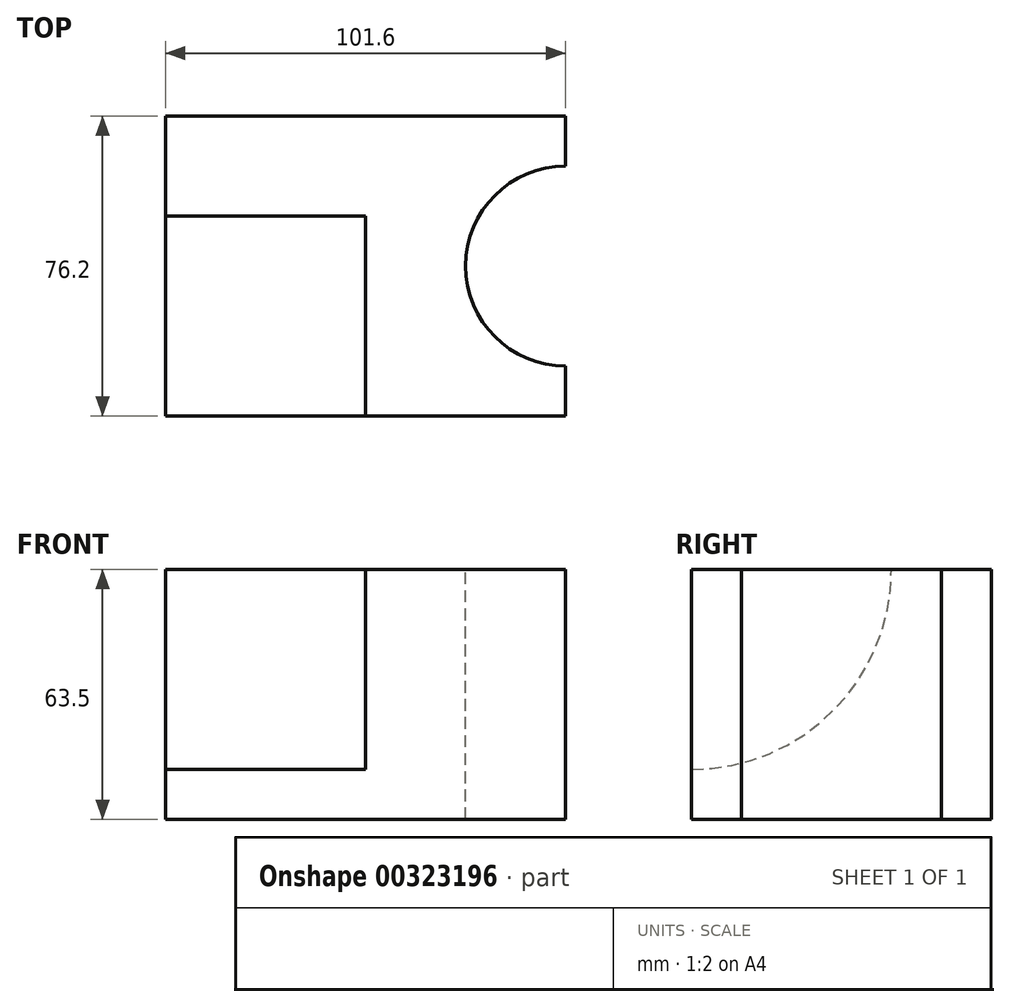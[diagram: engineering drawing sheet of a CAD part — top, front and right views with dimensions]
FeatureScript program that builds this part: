
annotation { "Feature Type Name" : "Feature", "Feature Type Description" : "" }
export const myFeature = defineFeature(function(context is Context, id is Id, definition is map)
    precondition{}
    {
        {
            var Q0;
            Q0=qCreatedBy(makeId("Front.planeOp"),FACE);
            var sketch = newSketch(context, id + "F0", { "sketchPlane" : qUnion([Q0])});
            skLineSegment(sketch, "E0", {"start": v(-51.32, -42.94) * mm, "end": v(50.28, -42.94) * mm});
            skLineSegment(sketch, "E1", {"start": v(50.28, -42.94) * mm, "end": v(50.28, 20.56) * mm});
            skLineSegment(sketch, "E2", {"start": v(50.28, 20.56) * mm, "end": v(-51.32, 20.56) * mm});
            skLineSegment(sketch, "E3", {"start": v(-51.32, 20.56) * mm, "end": v(-51.32, -42.94) * mm});
            skSolve(sketch);
        }
        {
            var Q0;
            Q0 = qSketchRegion(id + "F0", true);
            extrude(context, id + "F1", {"entities" : qUnion([Q0]), "oppositeDirection" : true, "depth" : 76.2 * mm});
        }
        {
            var Q0;
            Q0=makeQuery(id+"F1.opExtrude","SWEPT_FACE",FACE,{"disambiguationData":[OSD([sQuery(id+"F0.wireOp",EDGE,"E2")])]});
            var sketch = newSketch(context, id + "F2", { "sketchPlane" : qUnion([Q0])});
            skCircle(sketch, "E4", {"center": v(50.28, 38.1) * mm, "radius": 25.4 * mm});
            skSolve(sketch);
        }
        {
            var Q0;
            {var subQ0=sQuery(id+"F2.wireOp",EDGE,"E4");var subQ1=makeQuery(id+"F1.opExtrude","SWEPT_EDGE",EDGE,{"disambiguationData":[OSD([sQuery(id+"F0.wireOp",EDGE,"E1"),sQuery(id+"F0.wireOp",EDGE,"E2")])]});var subQ2=makeQuery(id+"F2.imprint","INTERSECT",VERTEX,{"disambiguationData":[OD(0.0)],"derivedFrom":[subQ1,subQ0]});Q0=makeQuery(id+"F2.imprint","IMPRINT",FACE,{"disambiguationData":[TD([[makeQuery(id+"F2.imprint","IMPRINT",EDGE,{"disambiguationData":[TD([[subQ2,-1.0]])],"derivedFrom":subQ0}),1.0]])]});}
            var Q1;
            {var subQ0=sQuery(id+"F2.wireOp",EDGE,"E4");var subQ1=makeQuery(id+"F1.opExtrude","SWEPT_EDGE",EDGE,{"disambiguationData":[OSD([sQuery(id+"F0.wireOp",EDGE,"E1"),sQuery(id+"F0.wireOp",EDGE,"E2")])]});var subQ2=makeQuery(id+"F2.imprint","INTERSECT",VERTEX,{"disambiguationData":[OD(0.0)],"derivedFrom":[subQ1,subQ0]});Q1=makeQuery(id+"F2.imprint","IMPRINT",FACE,{"disambiguationData":[TD([[makeQuery(id+"F2.imprint","IMPRINT",EDGE,{"disambiguationData":[TD([[subQ2,1.0]])],"derivedFrom":subQ0}),1.0]])]});}
            var Q2;
            Q2=sQuery(id+"F2.wireOp",EDGE,"E4");
            extrude(context, id + "F3", {"entities" : qUnion([Q0, Q1]), "operationType" : NewBodyOperationType.REMOVE, "surfaceEntities" : qUnion([Q2]), "oppositeDirection" : true, "depth" : 63.5 * mm});
        }
        {
            var Q0;
            Q0=makeQuery(id+"F1.opExtrude","SWEPT_FACE",FACE,{"disambiguationData":[OSD([sQuery(id+"F0.wireOp",EDGE,"E3")])]});
            var sketch = newSketch(context, id + "F4", { "sketchPlane" : qUnion([Q0])});
            skCircle(sketch, "E5", {"center": v(0, 20.56) * mm, "radius": 50.8 * mm});
            skSolve(sketch);
        }
        {
            var Q0;
            {var subQ0=sQuery(id+"F4.wireOp",EDGE,"E5");var subQ1=sQuery(id+"F0.wireOp",EDGE,"E3");var subQ4=makeQuery(id+"F1.opExtrude","CAP_EDGE",EDGE,{"disambiguationData":[OSD([subQ1])],"isStart":true});var subQ5=makeQuery(id+"F4.imprint","INTERSECT",VERTEX,{"derivedFrom":[subQ4,subQ0]});Q0=makeQuery(id+"F4.imprint","IMPRINT",FACE,{"disambiguationData":[TD([[makeQuery(id+"F4.imprint","IMPRINT",EDGE,{"disambiguationData":[TD([[subQ5,-1.0]])],"derivedFrom":subQ0}),1.0]])]});}
            var Q1;
            {var subQ0=sQuery(id+"F4.wireOp",EDGE,"E5");var subQ1=sQuery(id+"F0.wireOp",EDGE,"E3");var subQ4=makeQuery(id+"F1.opExtrude","CAP_EDGE",EDGE,{"disambiguationData":[OSD([subQ1])],"isStart":true});var subQ5=makeQuery(id+"F4.imprint","INTERSECT",VERTEX,{"derivedFrom":[subQ4,subQ0]});Q1=makeQuery(id+"F4.imprint","IMPRINT",FACE,{"disambiguationData":[TD([[makeQuery(id+"F4.imprint","IMPRINT",EDGE,{"disambiguationData":[TD([[subQ5,1.0]])],"derivedFrom":subQ0}),1.0]])]});}
            extrude(context, id + "F5", {"entities" : qUnion([Q0, Q1]), "operationType" : NewBodyOperationType.REMOVE, "oppositeDirection" : true, "depth" : 50.8 * mm});
        }
    });
